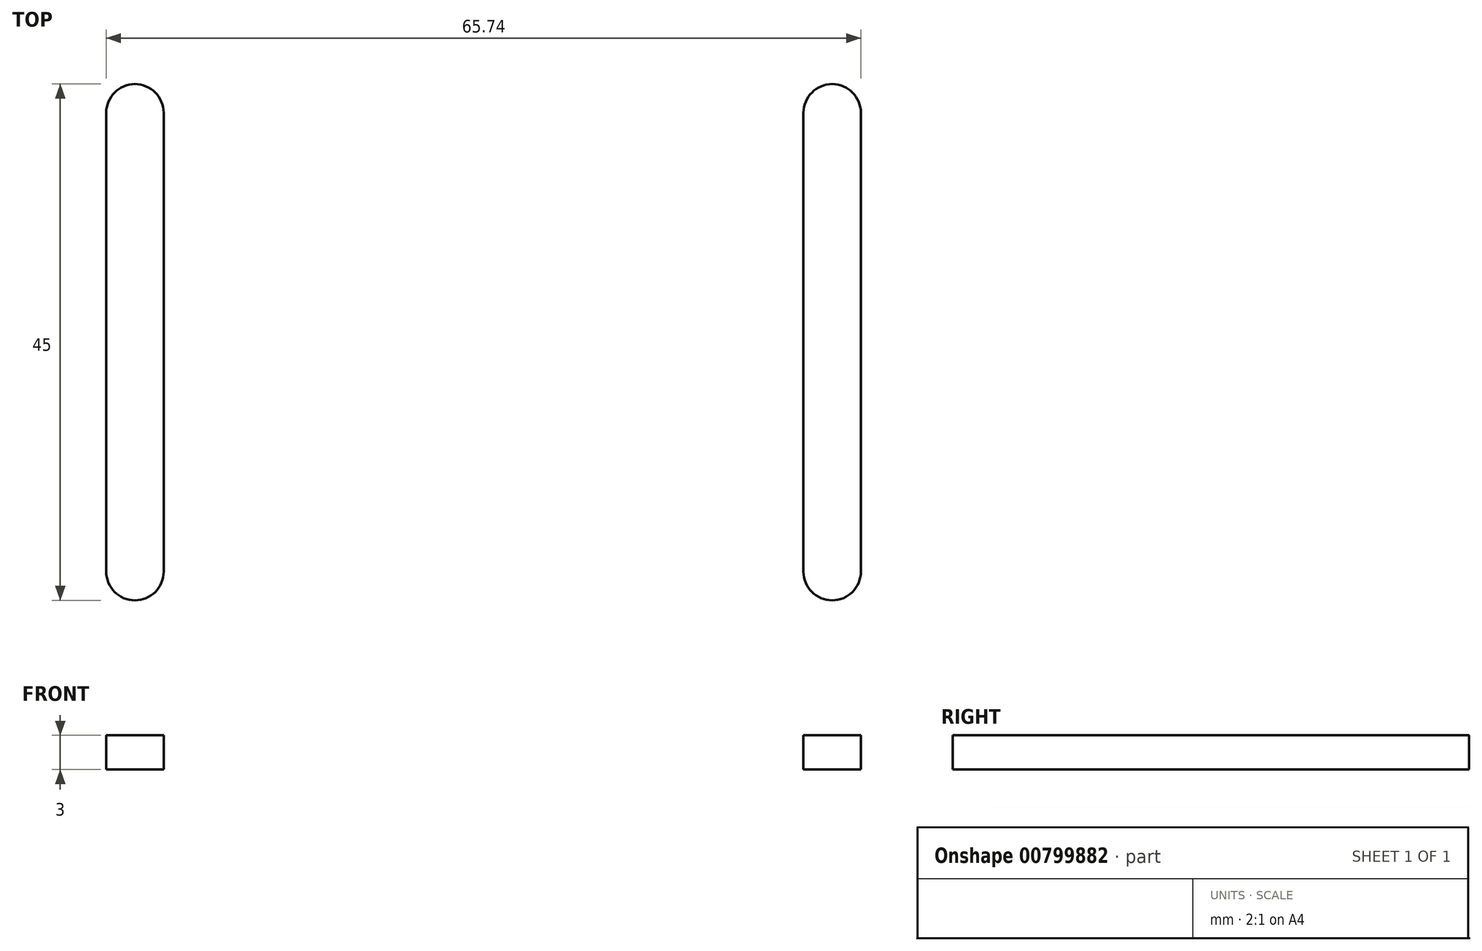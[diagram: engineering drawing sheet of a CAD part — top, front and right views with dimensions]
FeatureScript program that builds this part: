
annotation { "Feature Type Name" : "Feature", "Feature Type Description" : "" }
export const myFeature = defineFeature(function(context is Context, id is Id, definition is map)
    precondition{}
    {
        {
            var Q0;
            Q0=qCreatedBy(makeId("Top.planeOp"),FACE);
            var sketch = newSketch(context, id + "F0", { "sketchPlane" : qUnion([Q0])});
            skLineSegment(sketch, "E0.bottom", {"start": v(0, 0) * mm, "end": v(40.37, 0) * mm});
            skLineSegment(sketch, "E0.top", {"start": v(0, 100) * mm, "end": v(40.37, 100) * mm});
            skLineSegment(sketch, "E0.left", {"start": v(0, 0) * mm, "end": v(0, 100) * mm});
            skLineSegment(sketch, "E0.right", {"start": v(40.37, 0) * mm, "end": v(40.37, 100) * mm});
            skSolve(sketch);
        }
        {
            var Q0;
            Q0=makeQuery(id+"F0.imprint","IMPRINT",FACE,{"disambiguationData":[TD([[makeQuery(id+"F0.imprint","IMPRINT",EDGE,{"derivedFrom":sQuery(id+"F0.wireOp",EDGE,"E0.bottom")}),1.0]])]});
            extrude(context, id + "F1", {"entities" : qUnion([Q0]), "depth" : 3 * mm, "offsetDistance" : 25 * mm});
        }
        {
            var Q0;
            Q0=qCreatedBy(makeId("Top.planeOp"),FACE);
            var sketch = newSketch(context, id + "F2", { "sketchPlane" : qUnion([Q0])});
            skLineSegment(sketch, "E1", {"start": v(10.37, 25) * mm, "end": v(10.37, 50) * mm});
            skSolve(sketch);
        }
        {
            var Q0;
            Q0=sQuery(id+"F2.wireOp",VERTEX,"E1.start");
            var Q1;
            Q1=sQuery(id+"F2.wireOp",VERTEX,"E1.end");
            var Q2;
            Q2=makeQuery(id+"F1.opExtrude","SWEPT_BODY",BODY,{"disambiguationData":[OSD([sQuery(id+"F0.wireOp",EDGE,"E0.bottom"),sQuery(id+"F0.wireOp",EDGE,"E0.top"),sQuery(id+"F0.wireOp",EDGE,"E0.left"),sQuery(id+"F0.wireOp",EDGE,"E0.right")])]});
            hole(context, id + "F3", {"style" : HoleStyle.SIMPLE, "endStyle" : HoleEndStyle.THROUGH, "oppositeDirection" : true, "holeDiameter" : 3 * mm, "majorDiameter" : 5 * mm, "isTappedThrough" : true, "tappedDepth" : 12 * mm, "tapClearance" : 3, "locations" : qUnion([Q0, Q1]), "scope" : qUnion([Q2])});
        }
        {
            var Q0;
            Q0=makeQuery(id+"F1.opExtrude","CAP_FACE",FACE,{"disambiguationData":[OSD([sQuery(id+"F0.wireOp",EDGE,"E0.bottom"),sQuery(id+"F0.wireOp",EDGE,"E0.top"),sQuery(id+"F0.wireOp",EDGE,"E0.left"),sQuery(id+"F0.wireOp",EDGE,"E0.right")])],"isStart":false});
            var sketch = newSketch(context, id + "F4", { "sketchPlane" : qUnion([Q0])});
            skLineSegment(sketch, "E2", {"start": v(30.37, 20) * mm, "end": v(30.37, 60) * mm});
            skSolve(sketch);
        }
        {
            var Q0;
            Q0=makeQuery(id+"F1.opExtrude","SWEPT_EDGE",EDGE,{"disambiguationData":[OSD([sQuery(id+"F0.wireOp",EDGE,"E0.top"),sQuery(id+"F0.wireOp",EDGE,"E0.right")])]});
            var Q1;
            Q1=makeQuery(id+"F1.opExtrude","SWEPT_EDGE",EDGE,{"disambiguationData":[OSD([sQuery(id+"F0.wireOp",EDGE,"E0.bottom"),sQuery(id+"F0.wireOp",EDGE,"E0.right")])]});
            fillet(context, id + "F5", {"entities" : qUnion([Q0, Q1]), "radius" : 10 * mm, "tangentPropagation" : true, "allowEdgeOverflow" : false});
        }
        {
            var Q0;
            {var subQ3=sQuery(id+"F0.wireOp",EDGE,"E0.bottom");Q0=makeQuery(id+"F4.imprint","IMPRINT",FACE,{"disambiguationData":[TD([[makeQuery(id+"F4.imprint","IMPRINT",EDGE,{"derivedFrom":makeQuery(id+"F1.opExtrude","CAP_EDGE",EDGE,{"disambiguationData":[OSD([subQ3])],"isStart":false})}),1.0]])]});}
            var sketch = newSketch(context, id + "F6", { "sketchPlane" : qUnion([Q0])});
            skLineSegment(sketch, "E3.JTB.JTB", {"start": v(30.37, 20) * mm, "end": v(30.37, 60) * mm, "construction": true});
            skArc(sketch, "E3.0.startCap", {"start": v(32.87, 20) * mm, "mid": v(30.37, 17.5) * mm, "end": v(27.87, 20) * mm});
            skArc(sketch, "E3.0.endCap", {"start": v(27.87, 60) * mm, "mid": v(30.37, 62.5) * mm, "end": v(32.87, 60) * mm});
            skLineSegment(sketch, "E3.0.left", {"start": v(27.87, 20) * mm, "end": v(27.87, 60) * mm});
            skLineSegment(sketch, "E3.0.right", {"start": v(32.87, 20) * mm, "end": v(32.87, 60) * mm});
            skSolve(sketch);
        }
        {
            var Q0;
            Q0=makeQuery(id+"F6.imprint","IMPRINT",FACE,{"disambiguationData":[TD([[makeQuery(id+"F6.imprint","IMPRINT",EDGE,{"derivedFrom":sQuery(id+"F6.wireOp",EDGE,"E3.0.startCap")}),-1.0]])]});
            extrude(context, id + "F7", {"entities" : qUnion([Q0]), "operationType" : NewBodyOperationType.REMOVE, "oppositeDirection" : true, "depth" : 31.14 * mm, "offsetDistance" : 25 * mm});
        }
        {
            var Q0;
            Q0=makeQuery(id+"F1.opExtrude","SWEPT_BODY",BODY,{"disambiguationData":[OSD([sQuery(id+"F0.wireOp",EDGE,"E0.bottom"),sQuery(id+"F0.wireOp",EDGE,"E0.top"),sQuery(id+"F0.wireOp",EDGE,"E0.left"),sQuery(id+"F0.wireOp",EDGE,"E0.right")])]});
            var Q1;
            Q1=qCreatedBy(makeId("Right.planeOp"),FACE);
            mirror(context, id + "F8", {"operationType" : NewBodyOperationType.ADD, "entities" : qUnion([Q0]), "mirrorPlane" : qUnion([Q1])});
        }
    });
